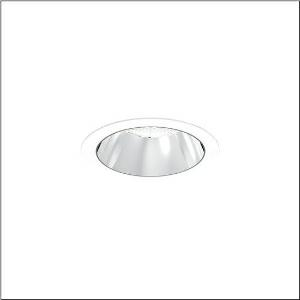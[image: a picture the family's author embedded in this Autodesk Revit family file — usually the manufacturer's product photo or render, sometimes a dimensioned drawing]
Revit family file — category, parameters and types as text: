
# Revit family: lunis_21_l_51db15ed91c
name_source: partatom
category: Lighting Fixtures
units: mm (PartAtom-declared; Revit-internal decimal feet)

## family parameters
Cut with Voids When Loaded = No
Host = Face
Light Source = No
Part Type = Normal
Room Calculation Point = No
Round Connector Dimension = Use Diameter
Shared = No

## types (1)
- --- (1 x LED, 4060 lm, 25.4 W, 6500K)
    Apparent Load = 25 VA
    CIE Flux Codes = 93 100 100 100 100
    Color Rendering = 80
    Color Temperature = 6500K
    Default Elevation = 1800 mm
    Description = Lunis 21 L, downlight, light control with lens, of PMMA, anti glare with reflector, of PC, highly specular, light emission: direct distribution, LED rated luminous flux: 2.120lm, light colour: 830/840/865, with terminal, 5-pole, mains connection: 220..240V, AC/DC, 0/50..60Hz, housing, round, of diecast aluminium, traffic white (RAL 9016), diameter: 165mm, clamping range: 1..40mm, protection rating (complete): IP20, protection rating (on room side): IP54, insulation class (complete): insulation class II (safety insulation), certification: CE, impact resistance: IK03, packaging unit: 1 piece
    Height = 0 mm  [stored 0 ft]
    Lamp = 1 x LED
    Lamp Light Flux = 4060 lm
    Lamp Power = 25.4 W
    Lamp count = 1
    Length = 165 mm
    Luminous efficacy = 160 lm/W
    Manufacturer = Siteco
    ModVariant = No
    Model = 51DB15ED91C
    Mounting Place = Ceiling
    Mounting Type = Recessed
    Number of Poles = 1
    OnlyDefault = Yes
    Power Factor = 1
    Product Name = Lunis 21 L
    Product group = downlight
    ProductGroupID = 401
    Protection Class = Protection class II
    Protection Degree = IP 20
    RLX_Detail_Level = 1
    RLX_Emergency_Light_Flux = 0 lm
    RLX_Emergency_Type = 0
    RLX_Emergency_Type_DB = No
    RlxData = <blob elided: 18257 chars, md5=203e2aee>
    Socket = socket
    Standby Power = 0 W
    System Light Flux = 4060 lm
    System Power = 25 W
    Type Comments = individual setting: colour temperature 6500K, luminous flux: 100 % | (ON | ON | OFF | OFF) | 700 mA
    Type Image = l_1291167.jpg
    URL = http://relux.com
    VarID = @adj_036273
    Voltage = 0 V
    Weight = 0.00 kg
    Width = 0 mm  [stored 0 ft]

note: [stored X ft] marks values corroborated as IEEE doubles in the binary element streams (Revit-internal decimal feet)

## geometry (parser evidence)
native form markers: Blend x4, Sweep x10
no freeform markers — native parametric forms only
